# Revit family: Faucet-Deck_Mount-Bath-KALLISTA-Fore_Town-P22731-1
name_source: partatom
category: Plumbing Fixtures
units: mm (PartAtom-declared; Revit-internal decimal feet)

## family parameters
Cut with Voids When Loaded = No
Host = Face
Maintain Annotation Orientation = No
OmniClass Number = 23.31.11.00
OmniClass Title = Faucets
Part Type = Normal
Room Calculation Point = No
Round Connector Dimension = Use Diameter
Shared = No

## types (4) — shared parameters
ADA Compliant = Yes
Assembly Code = D2010
CW Connection = Yes
Cold Water Inlet = Cold Water Inlet
Date Modified = 01/29/2025
Default Elevation = 36"
Description = Bathroom Sink Faucet, Low Spout
Drain Included = Yes
Flow Rate = 2 GPM
HW Connection = Yes
Handle Clearance = 2 3/4"
Height = 3 1/8"
Hot Water Inlet = Hot Water Inlet
Length = 4 3/4"
Manufacturer = Kallista Co.
Master Format 2014 = 22 41 39
Master Format 2014 Name = Residential Faucets, Supplies, and Trim
Material = Premium Metal Construction
Pressure = 60.00 psi
Product Documentation Link = https://resources.kohler.com
Product Name = Fore Town
Spout Reach = 4 3/4"
URL = https://www.kallista.com
Vent Connection = No
Waste Connection = No
Waste Water Outlet = Waste Water Outlet
WaterSense Certified = No

## per-type parameters (varying)
| type | Finish | Model | Product Page URL | Type |
| 24K-24K Gold | Kallista-Metal-24K-24K_Gold | P22731-24K |  | 1 |
| AD-Nickel Silver | Kallista-Metal-AD-Nickel_Silver | P22731-AD | https://www.kallista.com | 2 |
| CP-Chrome | Kallista-Metal-CP-Chrome | P22731-CP | https://www.kallista.com | 3 |
| LB-Bronze | Kallista-Metal-LB-Bronze | P22731-LB |  | 4 |

## geometry (parser evidence)
native form markers: Sweep x9
no freeform markers — native parametric forms only
